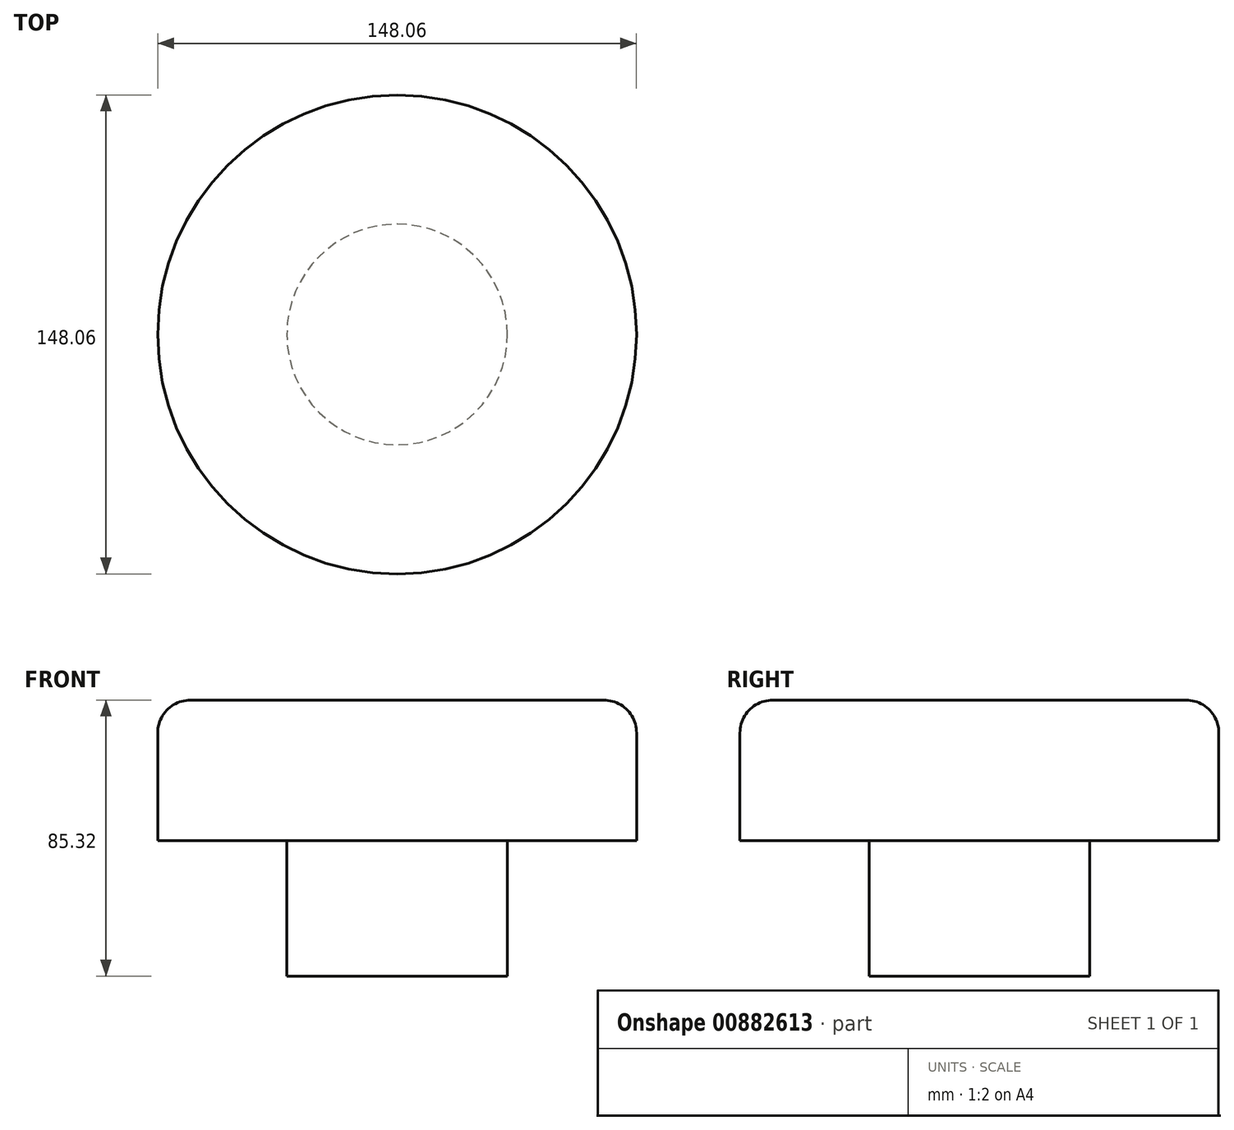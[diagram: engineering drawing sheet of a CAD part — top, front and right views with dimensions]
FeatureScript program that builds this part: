
annotation { "Feature Type Name" : "Feature", "Feature Type Description" : "" }
export const myFeature = defineFeature(function(context is Context, id is Id, definition is map)
    precondition{}
    {
        {
            var Q0;
            Q0=qCreatedBy(makeId("Front.planeOp"),FACE);
            var sketch = newSketch(context, id + "F0", { "sketchPlane" : qUnion([Q0])});
            skLineSegment(sketch, "E0.bottom", {"start": v(0, 0) * mm, "end": v(74.03, 0) * mm});
            skLineSegment(sketch, "E0.top", {"start": v(0, 43.4) * mm, "end": v(74.03, 43.4) * mm});
            skLineSegment(sketch, "E0.left", {"start": v(0, 0) * mm, "end": v(0, 43.4) * mm});
            skLineSegment(sketch, "E0.right", {"start": v(74.03, 0) * mm, "end": v(74.03, 43.4) * mm});
            skSolve(sketch);
        }
        {
            var Q0;
            Q0 = qSketchRegion(id + "F0", true);
            var Q1;
            Q1=sQuery(id+"F0.wireOp",EDGE,"E0.left");
            revolve(context, id + "F1", {"surfaceOperationType" : NewSurfaceOperationType.NEW, "entities" : qUnion([Q0]), "axis" : qUnion([Q1]), "revolveType" : RevolveType.FULL});
        }
        {
            var Q0;
            Q0=makeQuery(id+"F1.opRevolve","SWEPT_FACE",FACE,{"disambiguationData":[OSD([sQuery(id+"F0.wireOp",EDGE,"E0.bottom")])]});
            var sketch = newSketch(context, id + "F2", { "sketchPlane" : qUnion([Q0])});
            skCircle(sketch, "E1", {"center": v(0, 0) * mm, "radius": 34.1 * mm});
            skSolve(sketch);
        }
        {
            var Q0;
            Q0 = qSketchRegion(id + "F2", true);
            extrude(context, id + "F3", {"entities" : qUnion([Q0]), "operationType" : NewBodyOperationType.ADD, "depth" : 41.9 * mm, "offsetDistance" : 25.4 * mm});
        }
        {
            var Q0;
            Q0=makeQuery(id+"F1.opRevolve","SWEPT_EDGE",EDGE,{"disambiguationData":[OSD([sQuery(id+"F0.wireOp",EDGE,"E0.top"),sQuery(id+"F0.wireOp",EDGE,"E0.right")])]});
            fillet(context, id + "F4", {"entities" : qUnion([Q0]), "radius" : 10.16 * mm, "tangentPropagation" : true, "allowEdgeOverflow" : false});
        }
    });
